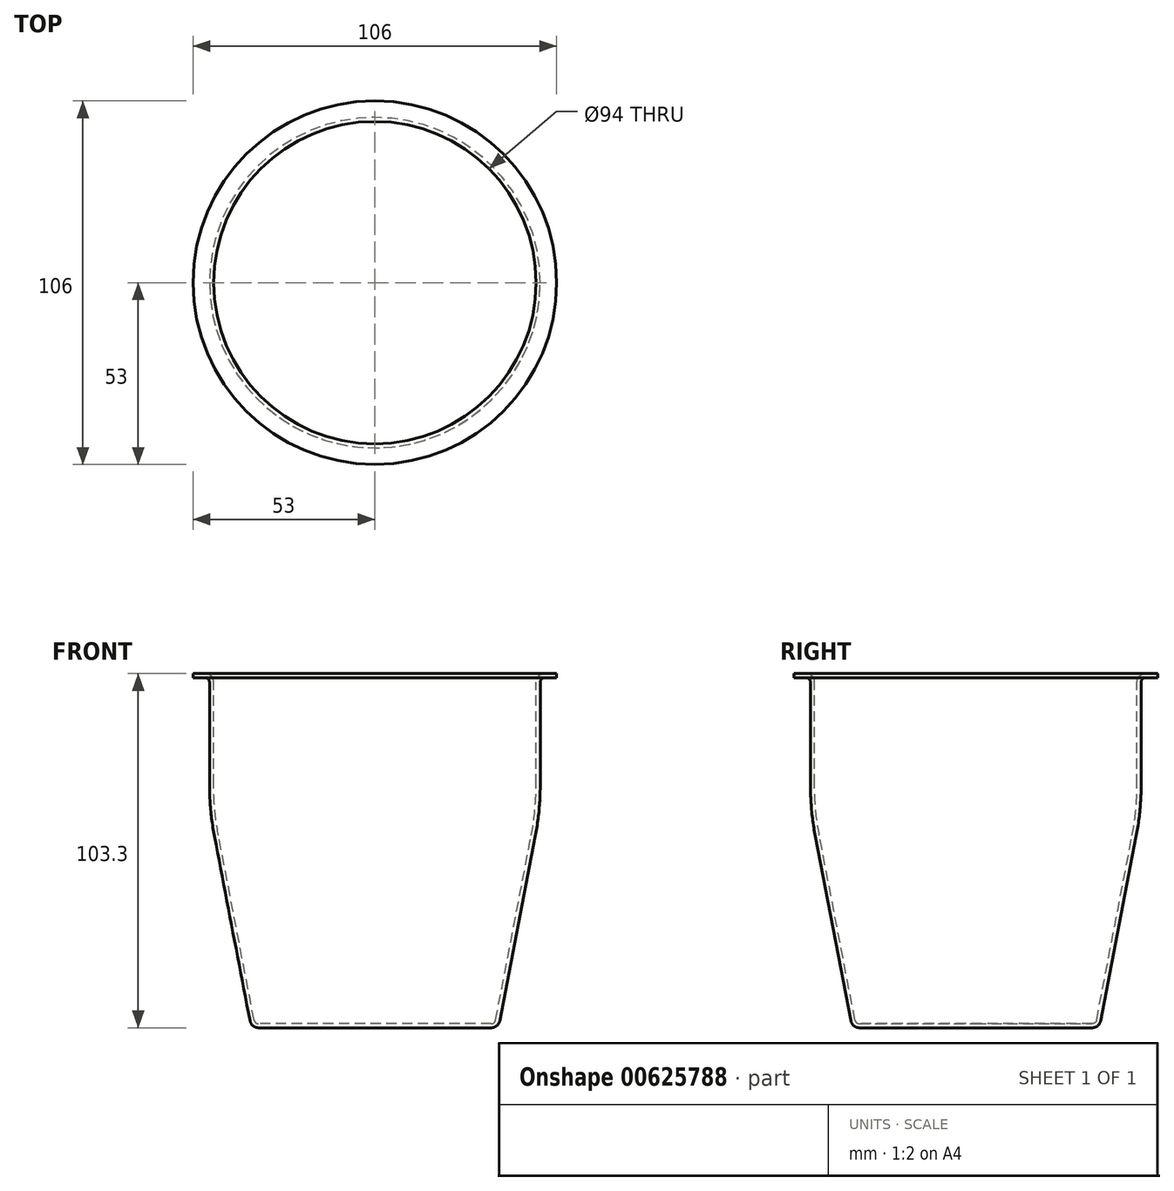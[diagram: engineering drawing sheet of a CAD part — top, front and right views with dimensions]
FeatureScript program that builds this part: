
annotation { "Feature Type Name" : "Feature", "Feature Type Description" : "" }
export const myFeature = defineFeature(function(context is Context, id is Id, definition is map)
    precondition{}
    {
        {
            var Q0;
            Q0=qCreatedBy(makeId("Front.planeOp"),FACE);
            var sketch = newSketch(context, id + "F0", { "sketchPlane" : qUnion([Q0])});
            skLineSegment(sketch, "E0", {"start": v(0, 0) * mm, "end": v(36, 0) * mm});
            skLineSegment(sketch, "E1", {"start": v(36, 0) * mm, "end": v(48.2, 63.3) * mm});
            skLineSegment(sketch, "E2", {"start": v(48.2, 63.3) * mm, "end": v(48.2, 102.1) * mm});
            skLineSegment(sketch, "E3", {"start": v(48.2, 102.1) * mm, "end": v(53, 102.1) * mm});
            skLineSegment(sketch, "E4", {"start": v(53, 102.1) * mm, "end": v(53, 103.3) * mm});
            skLineSegment(sketch, "E5", {"start": v(53, 103.3) * mm, "end": v(0, 103.3) * mm});
            skLineSegment(sketch, "E6", {"start": v(0, 103.3) * mm, "end": v(0, 0) * mm});
            skSolve(sketch);
        }
        {
            var Q0;
            Q0=makeQuery(id+"F0.imprint","IMPRINT",FACE,{"disambiguationData":[TD([[makeQuery(id+"F0.imprint","IMPRINT",EDGE,{"derivedFrom":sQuery(id+"F0.wireOp",EDGE,"E0")}),1.0]])]});
            var Q1;
            Q1=sQuery(id+"F0.wireOp",EDGE,"E6");
            revolve(context, id + "F1", {"surfaceOperationType" : NewSurfaceOperationType.NEW, "entities" : qUnion([Q0]), "axis" : qUnion([Q1]), "revolveType" : RevolveType.FULL});
        }
        {
            var Q0;
            Q0=makeQuery(id+"F1.opRevolve","SWEPT_EDGE",EDGE,{"disambiguationData":[OSD([sQuery(id+"F0.wireOp",EDGE,"E2"),sQuery(id+"F0.wireOp",EDGE,"E3")])]});
            fillet(context, id + "F2", {"entities" : qUnion([Q0]), "radius" : 1.3 * mm, "tangentPropagation" : true, "allowEdgeOverflow" : false});
        }
        {
            var Q0;
            Q0=makeQuery(id+"F1.opRevolve","SWEPT_EDGE",EDGE,{"disambiguationData":[OSD([sQuery(id+"F0.wireOp",EDGE,"E1"),sQuery(id+"F0.wireOp",EDGE,"E2")])]});
            fillet(context, id + "F3", {"entities" : qUnion([Q0]), "radius" : 80 * mm, "tangentPropagation" : true, "allowEdgeOverflow" : false});
        }
        {
            var Q0;
            Q0=makeQuery(id+"F1.opRevolve","SWEPT_EDGE",EDGE,{"disambiguationData":[OSD([sQuery(id+"F0.wireOp",EDGE,"E0"),sQuery(id+"F0.wireOp",EDGE,"E1")])]});
            fillet(context, id + "F4", {"entities" : qUnion([Q0]), "radius" : 2.5 * mm, "tangentPropagation" : true, "allowEdgeOverflow" : false});
        }
        {
            var Q0;
            Q0=makeQuery(id+"F1.opRevolve","SWEPT_FACE",FACE,{"disambiguationData":[OSD([sQuery(id+"F0.wireOp",EDGE,"E5")])]});
            shell(context, id + "F5", {"entities" : qUnion([Q0]), "thickness" : 1.2 * mm});
        }
    });
